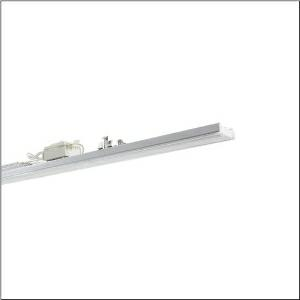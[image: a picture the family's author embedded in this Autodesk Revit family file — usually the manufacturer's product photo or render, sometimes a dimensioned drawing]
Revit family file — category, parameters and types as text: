
# Revit family: licross_r__11_recessed_mo_51tl147n48xg_3190
name_source: partatom
category: Lighting Fixtures
units: mm (PartAtom-declared; Revit-internal decimal feet)

## family parameters
Cut with Voids When Loaded = No
Host = Face
Light Source = No
Part Type = Normal
Room Calculation Point = No
Round Connector Dimension = Use Diameter
Shared = No

## types (1)
- Licross® 11 Recessed MO (1 x LED, 8240 lm, 48.5 W, 4000K)
    Apparent Load = 49 VA
    CIE Flux Codes = 56 84 97 100 100
    Color Rendering = 80
    Color Temperature = 4000K
    Default Elevation = 1800 mm
    Description = Licross® 11 Recessed MO, luminaire insert, of sheet steel, coil coated, white, length: 1.500mm, width: 66mm, height: 67mm, LED rated luminous flux: 8.240lm, light colour: 840, control gear: ON/OFF, with plug, 3-pole, with phase selection, mains connection: 220..240V, AC, 50/60Hz, rated input power: 49W, internal wiring halogen-free, primary light control with lens, of plastic, primary optical cover: cover, of PMMA, light emission: direct distribution, primary light characteristic: asymmetric, protection rating (complete): IP40, insulation class (complete): insulation class I (protective earthing), certification: CE, ENEC, VDE, UKCA, protection symbol: D if used in an environment without relevant dust loads with corresponding accessories, impact resistance: IK06, permissible ambient temperature for indoor applications: -35..+35°C, corresponds to IFS (International Featured Standards) requirements for safety and quality in the food industry, reducing of maximum allowable ambient temperature of 5°C with ceiling mounting, packaging unit: 1 piece
    Height = 58 mm
    Lamp = 1 x LED
    Lamp Light Flux = 8240 lm
    Lamp Power = 48.5 W
    Lamp count = 1
    Length = 1500 mm
    Luminous efficacy = 170 lm/W
    Manufacturer = Siteco
    ModVariant = No
    Model = 51TL147N48XG
    Mounting Place = Ceiling
    Mounting Type = Pendant
    Number of Poles = 1
    OnlyDefault = Yes
    Power Factor = 1
    Product Name = Licross® 11 Recessed MO
    Product group = luminaire insert | ceiling pendant
    ProductGroupID = 902
    Protection Class = Protection class I
    Protection Degree = IP 40
    RLX_Detail_Level = 1
    RLX_Emergency_Light_Flux = 0 lm
    RLX_Emergency_Type = 0
    RLX_Emergency_Type_DB = No
    RlxData = <blob elided: 21309 chars, md5=1fe5f05d>
    Socket = socket
    Standby Power = 0 W
    System Light Flux = 8240 lm
    System Power = 49 W
    Type Comments = Product without accessories
    Type Image = l_1296930.jpg
    URL = http://relux.com
    VarID = ---
    Voltage = 0 V
    Weight = 0.00 kg
    Width = 66 mm

## geometry (parser evidence)
native form markers: Blend x4, Sweep x11
no freeform markers — native parametric forms only
